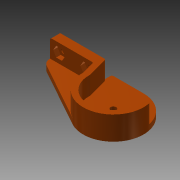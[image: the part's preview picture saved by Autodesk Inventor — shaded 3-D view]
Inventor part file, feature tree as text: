
AUTODESK INVENTOR PART (.ipt)
format: ipt  version: 2013 (Build 170138000, 138)  size: 221,696 bytes
history: native  units: mm
features: extrude x10, sketch x10, fillet x1
ambient origin geometry x8: Origin, YZ Plane, XZ Plane, XY Plane, X Axis, Y Axis, Z Axis, Center Point
bodies: Solid1 (feature_tree)
feature tree (21):
  extrude  "Extrusion1"  Depth=12.5mm
  extrude  "Extrusion2"  Depth=20.0mm
  extrude  "Extrusion3"  Depth=5.0mm
  extrude  "Extrusion4"  Depth=5.0mm
  extrude  "Extrusion5"  Depth=5.0mm
  fillet  "Fillet1"  Radius=27.33mm
  extrude  "Extrusion6"  Depth=26.0mm
  extrude  "Extrusion7"  Depth=10.0mm TaperAngle=0.0deg
  extrude  "Extrusion8"  Depth=10.0mm TaperAngle=0.0deg
  extrude  "Extrusion9"  Depth=1.0mm
  extrude  "Extrusion10"  Depth=2.1mm TaperAngle=0.0deg
  sketch  "Sketch1"  dims[d0=26.33mm d2=12.5mm]
  sketch  "Sketch2"  dims[d3=22.5mm d4=20.0mm]
  sketch  "Sketch3"  dims[d5=25.0mm d6=5.0mm]
  sketch  "Sketch4"  dims[d8=3.5mm d9=5.0mm]
  sketch  "Sketch5"  dims[d10=3.0mm d11=0.0mm d12=5.0mm d14=27.33mm]
  sketch  "Sketch6"  dims[d15=10.0mm d16=0.0mm d17=26.0mm]
  sketch  "Sketch7"  dims[d19=30.0deg d21=10.0mm d22=0.0mm]
  sketch  "Sketch8"  dims[d23=3.0mm d24=10.0mm d25=0.0mm]
  sketch  "Sketch9"  dims[d26=10.0mm d27=0.0mm d28=1.0mm]
  sketch  "Sketch10"  dims[d29=3.1mm d31=2.1mm d32=0.0mm d33=5.6mm d34=2.5mm d35=0.0mm d36=5.0mm d37=15.0mm d38=3.1mm d39=2.5mm d40=0.0mm d41=5.6mm d42=5.0mm d43=0.0mm d44=15.0mm d46=1.0mm d47=0.0mm]
